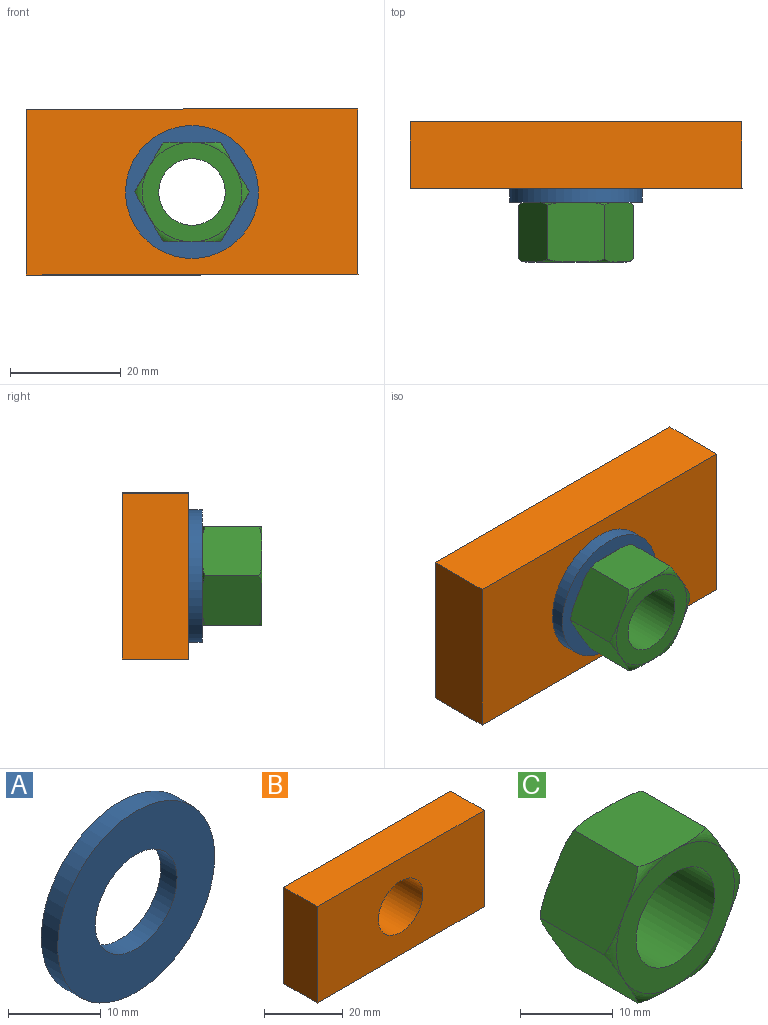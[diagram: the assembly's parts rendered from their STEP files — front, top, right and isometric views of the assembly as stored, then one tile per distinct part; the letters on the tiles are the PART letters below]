
ASSEMBLY  parts=3 mates=2
PART A: 4 faces, bbox 24x2.5x24 mm
  f0: cylinder r=6.25mm len=12.5mm, axis (0,1,0), area 98.2mm2, adj f2,f3
  f1: cylinder r=12mm len=24mm, axis (0,1,0), area 188.5mm2, adj f2,f3
  f2: plane 24x24mm, normal (0,-1,0), area 329.7mm2, adj f0,f1
  f3: plane 24x24mm, normal (0,1,0), area 329.7mm2, adj f0,f1
PART B: 7 faces, bbox 60x12x30 mm
  f0: plane 30x12mm, normal (-1,0,0), area 360mm2, adj f1,f3,f5,f6
  f1: plane 60x12mm, normal (0,0,-1), area 720mm2, adj f0,f2,f5,f6
  f2: plane 30x12mm, normal (1,0,0), area 360mm2, adj f1,f3,f5,f6
  f3: plane 60x12mm, normal (0,0,1), area 720mm2, adj f0,f2,f5,f6
  f4: cylinder r=8mm len=16mm, axis (0,1,0), area 603.2mm2, adj f5,f6
  f5: plane 60x30mm, normal (0,-1,0), area 1598.9mm2, adj f0,f1,f2,f3,f4
  f6: plane 60x30mm, normal (0,1,0), area 1598.9mm2, adj f0,f1,f2,f3,f4
PART C: 21 faces, bbox 22.6x10.8x22.6 mm
  f0: plane 10.8x10.4mm, normal (0,0,1), area 110mm2, adj f1,f5,f10,f14,f15,f20
  f1: plane 10.8x9mm, normal (-0.87,0,0.5), area 110mm2, adj f0,f2,f13,f14,f19,f20
  f2: plane 10.8x9mm, normal (-0.87,0,-0.5), area 110mm2, adj f1,f3,f12,f13,f18,f19
  f3: plane 10.8x10.4mm, normal (0,0,-1), area 110mm2, adj f2,f4,f11,f12,f17,f18
  f4: plane 10.8x9mm, normal (0.87,0,-0.5), area 110mm2, adj f3,f5,f9,f11,f16,f17
  f5: plane 10.8x9mm, normal (0.87,0,0.5), area 110mm2, adj f0,f4,f9,f10,f15,f16
  f6: plane 18x18mm, normal (0,1,0), area 141.4mm2, adj f8,f15,f16,f17,f18,f19,f20
  f7: plane 18x18mm, normal (0,-1,0), area 141.4mm2, adj f8,f9,f10,f11,f12,f13,f14
  f8: cylinder r=6mm len=12mm, axis (0,1,0), area 407.2mm2, adj f6,f7
  f9: torus R=9mm, axis (0,-1,0), area 4.5mm2, adj f4,f5,f7
  f10: torus R=9mm, axis (0,-1,0), area 4.5mm2, adj f0,f5,f7
  f11: torus R=9mm, axis (0,-1,0), area 4.5mm2, adj f3,f4,f7
  f12: torus R=9mm, axis (0,-1,0), area 4.5mm2, adj f2,f3,f7
  f13: torus R=9mm, axis (0,-1,0), area 4.5mm2, adj f1,f2,f7
  f14: torus R=9mm, axis (0,-1,0), area 4.5mm2, adj f0,f1,f7
  f15: torus R=9mm, axis (0,1,0), area 4.5mm2, adj f0,f5,f6
  f16: torus R=9mm, axis (0,1,0), area 4.5mm2, adj f4,f5,f6
  f17: torus R=9mm, axis (0,1,0), area 4.5mm2, adj f3,f4,f6
  f18: torus R=9mm, axis (0,1,0), area 4.5mm2, adj f2,f3,f6
  f19: torus R=9mm, axis (0,1,0), area 4.5mm2, adj f1,f2,f6
  f20: torus R=9mm, axis (0,1,0), area 4.5mm2, adj f0,f1,f6
PLACE A t=(9.26,-4.25,5.65)mm
PLACE B t=(-24.43,7.75,-9.35)mm
PLACE C t=(5.57,-12.15,5.65)mm
MATE fastened A.f0 <-> B.f4  axis (0,1,0) through (5.57,-4.25,5.65)mm
MATE fastened C.f8 <-> A.f0  axis (0,1,0) through (5.57,-6.75,5.65)mm
